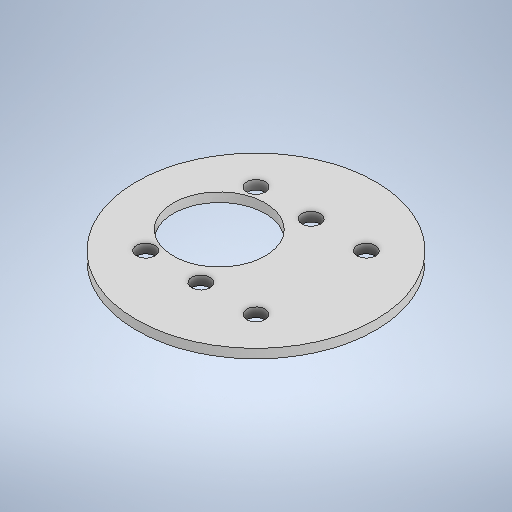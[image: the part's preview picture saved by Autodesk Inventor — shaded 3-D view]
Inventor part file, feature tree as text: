
AUTODESK INVENTOR PART (.ipt)
format: ipt  version: 2025.1 (Build 291241000, 241)  size: 268,800 bytes
history: native  units: mm
features: extrude x2, sketch x2
ambient origin geometry x8: Origin, YZ Plane, XZ Plane, XY Plane, X Axis, Y Axis, Z Axis, Center Point
bodies: Solid1 (feature_tree)
feature tree (4):
  extrude  "Extrusion1"  Depth=2.0mm
  extrude  "Extrusion2"  Depth=6.0mm
  sketch  "Sketch1"  dims[d0=26.0mm d2=2.0mm]
  sketch  "Sketch2"  dims[d3=12.0mm d4=6.0mm d5=12.0mm d6=6.0mm d7=6.0mm d8=2.0mm d9=1.0mm d10=0.0mm d11=10.0mm d12=4.0mm d13=18.0mm d14=0.0mm]
